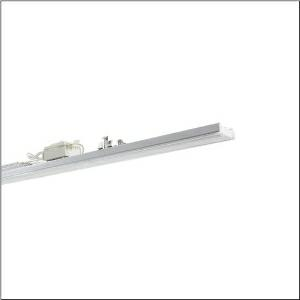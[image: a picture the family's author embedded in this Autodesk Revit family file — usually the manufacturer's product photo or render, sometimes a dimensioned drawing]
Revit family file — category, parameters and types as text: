
# Revit family: licross_r__21_recessed_mo_52te1e7n485g_828a
name_source: partatom
category: Lighting Fixtures
units: mm (PartAtom-declared; Revit-internal decimal feet)

## family parameters
Cut with Voids When Loaded = No
Host = Face
Light Source = No
Part Type = Normal
Room Calculation Point = No
Round Connector Dimension = Use Diameter
Shared = No

## types (1)
- Licross® 21 Recessed MO (1 x LED, 8530 lm, 47.9 W, 4000K)
    Apparent Load = 48 VA
    CIE Flux Codes = 85 95 99 100 100
    Color Rendering = 80
    Color Temperature = 4000K
    Default Elevation = 1800 mm
    Description = Licross® 21 Recessed MO, luminaire insert, of sheet steel, galvanised, coil coated, white, length: 1.500mm, width: 66mm, height: 67mm, LED rated luminous flux: 8.530lm, light colour: 840, control gear: ON/OFF, with plug, 3-pole, with phase selection, mains connection: 220..240V, AC, 50/60Hz, rated input power: 48W, halogen-free wiring, primary light control with lens, of plastic, primary optical cover: cover, of PMMA, light emission: direct distribution, primary light characteristic: symmetric, protection rating (complete): IP54, insulation class (complete): insulation class I (protective earthing), certification: CE, ENEC, VDE, UKCA, protection symbol: D if used in an environment with non-conductive dust loads with corresponding accessories, impact resistance: IK06, permissible ambient temperature for indoor applications: -35..+40°C, corresponds to IFS (International Featured Standards) requirements for safety and quality in the food industry, reducing of maximum allowable ambient temperature of 5°C with ceiling mounting, LABS conformity tested according to VDMA 24364:2018-05, packaging unit: 1 piece
    Height = 58 mm
    Lamp = 1 x LED
    Lamp Light Flux = 8530 lm
    Lamp Power = 47.9 W
    Lamp count = 1
    Length = 1500 mm
    Luminous efficacy = 178 lm/W
    Manufacturer = Siteco
    ModVariant = No
    Model = 52TE1E7N485G
    Mounting Place = Ceiling
    Mounting Type = Pendant
    Number of Poles = 1
    OnlyDefault = Yes
    Power Factor = 1
    Product Name = Licross® 21 Recessed MO
    Product group = luminaire insert
    ProductGroupID = 902
    Protection Class = Protection class I
    Protection Degree = IP 54
    RLX_Detail_Level = 1
    RLX_Emergency_Light_Flux = 0 lm
    RLX_Emergency_Type = 0
    RLX_Emergency_Type_DB = No
    RlxData = <blob elided: 20973 chars, md5=32fc530b>
    Socket = socket
    Standby Power = 0 W
    System Light Flux = 8530 lm
    System Power = 48 W
    Type Comments = Product without accessories
    Type Image = l_1296930.jpg
    URL = http://relux.com
    VarID = ---
    Voltage = 0 V
    Weight = 0.00 kg
    Width = 66 mm

## geometry (parser evidence)
native form markers: Blend x4, Sweep x12
no freeform markers — native parametric forms only
